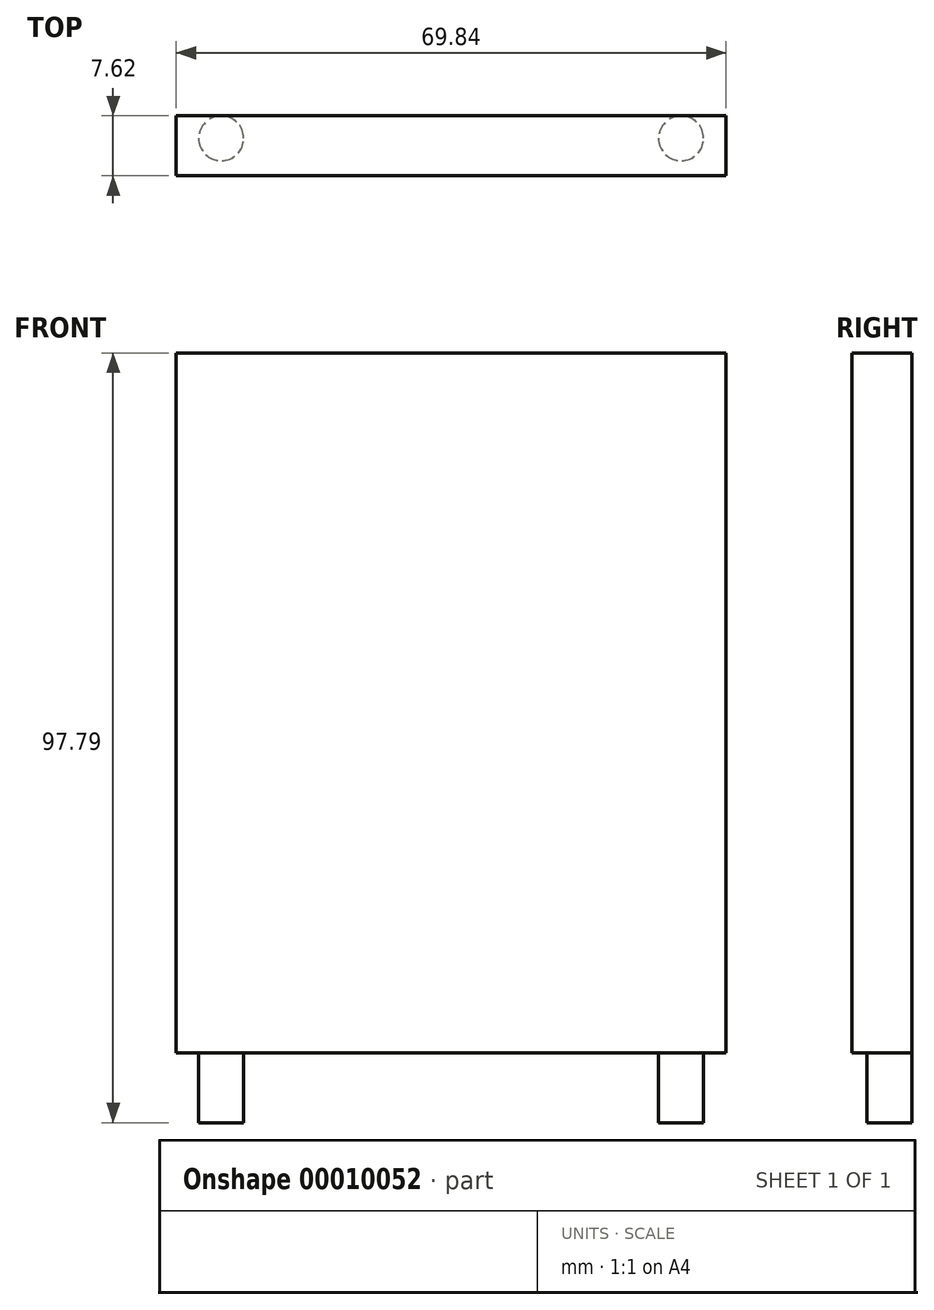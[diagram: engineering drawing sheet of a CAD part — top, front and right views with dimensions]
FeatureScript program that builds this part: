
annotation { "Feature Type Name" : "Feature", "Feature Type Description" : "" }
export const myFeature = defineFeature(function(context is Context, id is Id, definition is map)
    precondition{}
    {
        {
            var Q0;
            Q0=qCreatedBy(makeId("Front.planeOp"),FACE);
            var sketch = newSketch(context, id + "F0", { "sketchPlane" : qUnion([Q0])});
            skLineSegment(sketch, "E0.bottom", {"start": v(-34.93, 44.45) * mm, "end": v(34.93, 44.45) * mm});
            skLineSegment(sketch, "E0.top", {"start": v(-34.93, -44.45) * mm, "end": v(34.93, -44.45) * mm});
            skLineSegment(sketch, "E0.left", {"start": v(-34.93, 44.45) * mm, "end": v(-34.92, -44.45) * mm});
            skLineSegment(sketch, "E0.right", {"start": v(34.93, 44.45) * mm, "end": v(34.93, -44.45) * mm});
            skPoint(sketch, "E1", {"position": v(-27.6, -44.45) * mm});
            skPoint(sketch, "E2", {"position": v(27.6, -44.45) * mm});
            skSolve(sketch);
        }
        {
            var Q0;
            Q0=makeQuery(id+"F0.imprint","IMPRINT",FACE,{"disambiguationData":[TD([[makeQuery(id+"F0.imprint","IMPRINT",EDGE,{"derivedFrom":sQuery(id+"F0.wireOp",EDGE,"E0.bottom")}),-1.0]])]});
            extrude(context, id + "F1", {"entities" : qUnion([Q0]), "depth" : 7.62 * mm});
        }
        {
            var Q0;
            Q0=makeQuery(id+"F1.opExtrude","SWEPT_FACE",FACE,{"disambiguationData":[OSD([sQuery(id+"F0.wireOp",EDGE,"E0.top")])]});
            var sketch = newSketch(context, id + "F2", { "sketchPlane" : qUnion([Q0])});
            skCircle(sketch, "E3", {"center": v(-29.2, 2.86) * mm, "radius": 2.86 * mm});
            skCircle(sketch, "E4", {"center": v(29.21, 2.86) * mm, "radius": 2.86 * mm});
            skLineSegment(sketch, "E5", {"start": v(-29.2, 2.86) * mm, "end": v(0, 0) * mm});
            skLineSegment(sketch, "E6", {"start": v(0, 0) * mm, "end": v(29.21, 2.86) * mm});
            skSolve(sketch);
        }
        {
            var Q0;
            {var subQ0=sQuery(id+"F2.wireOp",EDGE,"E3");var subQ1=sQuery(id+"F0.wireOp",EDGE,"E0.top");var subQ3=makeQuery(id+"F2.imprint","INTERSECT",VERTEX,{"derivedFrom":[makeQuery(id+"F1.opExtrude","CAP_EDGE",EDGE,{"disambiguationData":[OSD([subQ1])],"isStart":true}),subQ0]});Q0=makeQuery(id+"F2.imprint","IMPRINT",FACE,{"disambiguationData":[TD([[makeQuery(id+"F2.imprint","IMPRINT",EDGE,{"disambiguationData":[TD([[subQ3,1.0]])],"derivedFrom":subQ0}),1.0]])]});}
            var Q1;
            {var subQ0=sQuery(id+"F2.wireOp",EDGE,"E4");var subQ1=sQuery(id+"F0.wireOp",EDGE,"E0.top");var subQ3=makeQuery(id+"F2.imprint","INTERSECT",VERTEX,{"derivedFrom":[makeQuery(id+"F1.opExtrude","CAP_EDGE",EDGE,{"disambiguationData":[OSD([subQ1])],"isStart":true}),subQ0]});Q1=makeQuery(id+"F2.imprint","IMPRINT",FACE,{"disambiguationData":[TD([[makeQuery(id+"F2.imprint","IMPRINT",EDGE,{"disambiguationData":[TD([[subQ3,1.0]])],"derivedFrom":subQ0}),1.0]])]});}
            extrude(context, id + "F3", {"entities" : qUnion([Q0, Q1]), "operationType" : NewBodyOperationType.ADD, "depth" : 8.9 * mm});
        }
    });
